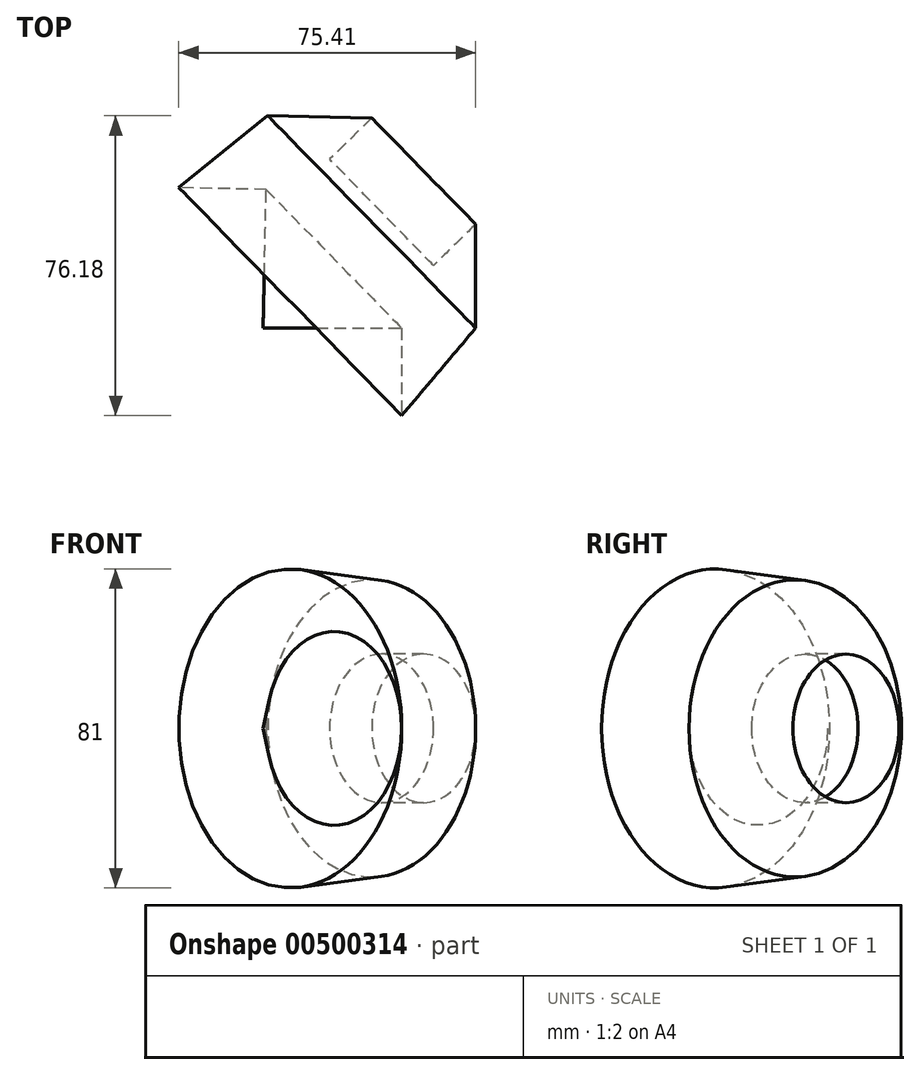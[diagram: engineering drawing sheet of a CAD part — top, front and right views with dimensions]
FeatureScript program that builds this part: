
annotation { "Feature Type Name" : "Feature", "Feature Type Description" : "" }
export const myFeature = defineFeature(function(context is Context, id is Id, definition is map)
    precondition{}
    {
        {
            var Q0;
            Q0=qCreatedBy(makeId("Top.planeOp"),FACE);
            var sketch = newSketch(context, id + "F0", { "sketchPlane" : qUnion([Q0])});
            skLineSegment(sketch, "E0", {"start": v(-35.22, 0) * mm, "end": v(-5.13, 29.44) * mm});
            skLineSegment(sketch, "E1", {"start": v(-5.13, 29.44) * mm, "end": v(8.07, 15.95) * mm});
            skLineSegment(sketch, "E2", {"start": v(8.07, 15.95) * mm, "end": v(18.77, 26.41) * mm});
            skLineSegment(sketch, "E3", {"start": v(18.77, 26.41) * mm, "end": v(18.77, 0) * mm});
            skLineSegment(sketch, "E4", {"start": v(18.77, 0) * mm, "end": v(0, -22.2) * mm});
            skLineSegment(sketch, "E5", {"start": v(0, -22.2) * mm, "end": v(0, 0) * mm});
            skLineSegment(sketch, "E6", {"start": v(0, 0) * mm, "end": v(-35.22, 0) * mm});
            skSolve(sketch);
        }
        {
            var Q0;
            Q0=makeQuery(id+"F0.imprint","IMPRINT",FACE,{"disambiguationData":[TD([[makeQuery(id+"F0.imprint","IMPRINT",EDGE,{"derivedFrom":sQuery(id+"F0.wireOp",EDGE,"E0")}),-1.0]])]});
            var Q1;
            Q1=sQuery(id+"F0.wireOp",EDGE,"E0");
            revolve(context, id + "F1", {"entities" : qUnion([Q0]), "axis" : qUnion([Q1]), "revolveType" : RevolveType.FULL});
        }
    });
